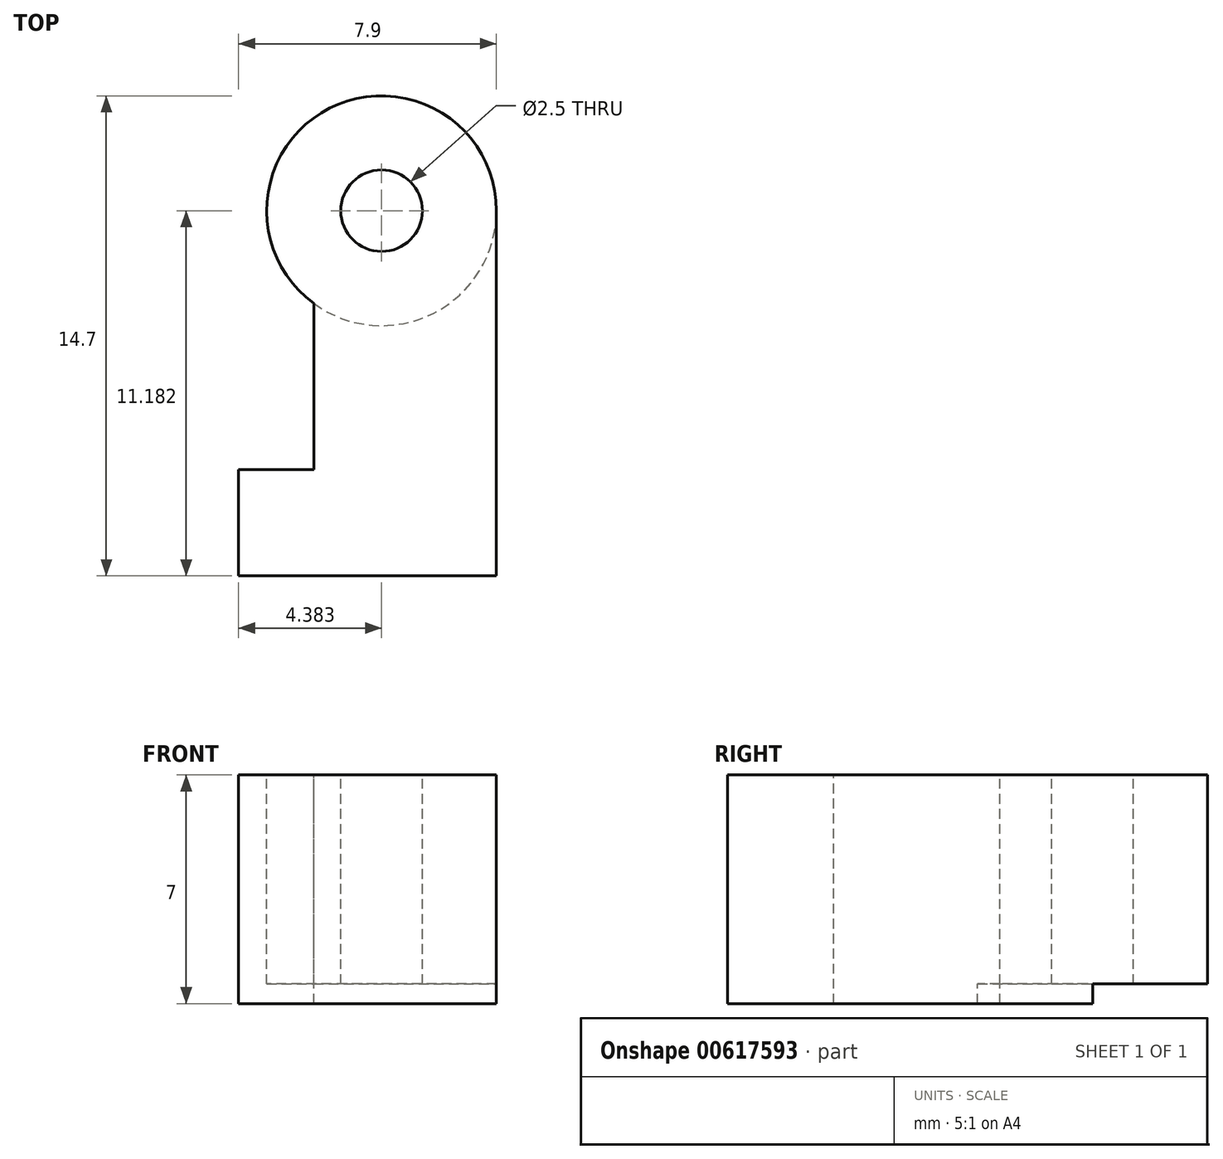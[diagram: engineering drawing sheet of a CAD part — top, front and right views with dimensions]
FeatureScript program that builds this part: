
annotation { "Feature Type Name" : "Feature", "Feature Type Description" : "" }
export const myFeature = defineFeature(function(context is Context, id is Id, definition is map)
    precondition{}
    {
        {
            var Q0;
            Q0=qCreatedBy(makeId("Top.planeOp"),FACE);
            var sketch = newSketch(context, id + "F0", { "sketchPlane" : qUnion([Q0])});
            skCircle(sketch, "E0", {"center": v(-3.47, -3.53) * mm, "radius": 3.52 * mm});
            skLineSegment(sketch, "E1", {"start": v(-3.47, 0) * mm, "end": v(-3.47, -14.7) * mm, "construction": true});
            skLineSegment(sketch, "E2", {"start": v(-3.47, -14.7) * mm, "end": v(0.05, -14.7) * mm});
            skLineSegment(sketch, "E3", {"start": v(0.05, -14.7) * mm, "end": v(0.05, -3.53) * mm});
            skLineSegment(sketch, "E4", {"start": v(-3.47, -14.7) * mm, "end": v(-7.85, -14.7) * mm});
            skLineSegment(sketch, "E5", {"start": v(-7.85, -14.7) * mm, "end": v(-7.85, -11.46) * mm});
            skLineSegment(sketch, "E6", {"start": v(-7.85, -11.46) * mm, "end": v(-5.55, -11.46) * mm});
            skLineSegment(sketch, "E7", {"start": v(-5.55, -11.46) * mm, "end": v(-5.55, -6.37) * mm});
            skCircle(sketch, "E8", {"center": v(-3.47, -3.53) * mm, "radius": 1.25 * mm});
            skSolve(sketch);
        }
        {
            var Q0;
            Q0=makeQuery(id+"F0.imprint","IMPRINT",FACE,{"disambiguationData":[TD([[makeQuery(id+"F0.imprint","IMPRINT",EDGE,{"derivedFrom":sQuery(id+"F0.wireOp",EDGE,"E2")}),1.0]])]});
            extrude(context, id + "F1", {"entities" : qUnion([Q0]), "oppositeDirection" : true, "depth" : 7 * mm, "offsetDistance" : 25 * mm});
        }
        {
            var Q0;
            Q0=makeQuery(id+"F0.imprint","IMPRINT",FACE,{"disambiguationData":[TD([[makeQuery(id+"F0.imprint","IMPRINT",EDGE,{"derivedFrom":sQuery(id+"F0.wireOp",EDGE,"E8")}),-1.0]])]});
            extrude(context, id + "F2", {"entities" : qUnion([Q0]), "operationType" : NewBodyOperationType.ADD, "oppositeDirection" : true, "depth" : 6.4 * mm, "offsetDistance" : 25 * mm});
        }
    });
